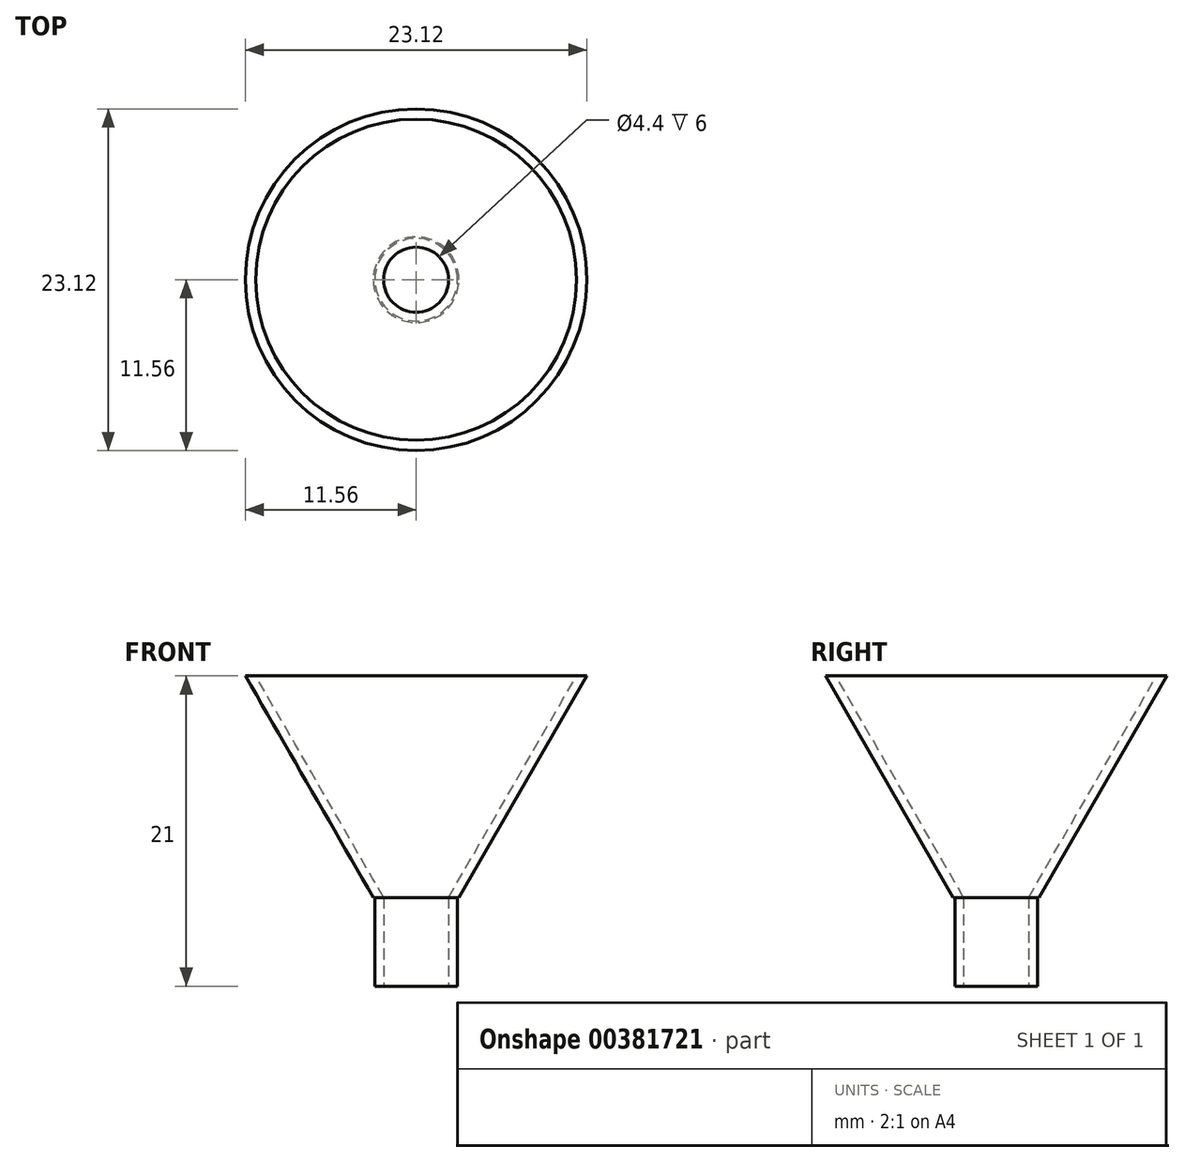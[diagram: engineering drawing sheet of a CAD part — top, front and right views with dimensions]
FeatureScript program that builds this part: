
annotation { "Feature Type Name" : "Feature", "Feature Type Description" : "" }
export const myFeature = defineFeature(function(context is Context, id is Id, definition is map)
    precondition{}
    {
        {
            var Q0;
            Q0=qCreatedBy(makeId("Top.planeOp"),FACE);
            var sketch = newSketch(context, id + "F0", { "sketchPlane" : qUnion([Q0])});
            skCircle(sketch, "E0", {"center": v(0, 0) * mm, "radius": 2.8 * mm});
            skCircle(sketch, "E1", {"center": v(0, 0) * mm, "radius": 2.2 * mm});
            skSolve(sketch);
        }
        {
            var Q0;
            Q0 = qSketchRegion(id + "F0", true);
            extrude(context, id + "F1", {"entities" : qUnion([Q0]), "depth" : 6 * mm});
        }
        {
            var Q0;
            Q0=qCreatedBy(makeId("Front.planeOp"),FACE);
            var sketch = newSketch(context, id + "F2", { "sketchPlane" : qUnion([Q0])});
            skLineSegment(sketch, "E2.0", {"start": v(-2.2, 6) * mm, "end": v(2.2, 6) * mm, "construction": true});
            skLineSegment(sketch, "E3", {"start": v(2.2, 6) * mm, "end": v(10.86, 21) * mm});
            skLineSegment(sketch, "E4", {"start": v(10.86, 21) * mm, "end": v(11.56, 21) * mm});
            skLineSegment(sketch, "E5", {"start": v(11.56, 21) * mm, "end": v(2.9, 6) * mm});
            skLineSegment(sketch, "E6", {"start": v(2.9, 6) * mm, "end": v(2.2, 6) * mm});
            skLineSegment(sketch, "E7", {"start": v(0, 6) * mm, "end": v(0, 24.89) * mm});
            skSolve(sketch);
        }
        {
            var Q0;
            Q0=makeQuery(id+"F2.imprint","IMPRINT",FACE,{"disambiguationData":[TD([[makeQuery(id+"F2.imprint","IMPRINT",EDGE,{"derivedFrom":sQuery(id+"F2.wireOp",EDGE,"E3")}),-1.0]])]});
            var Q1;
            Q1=sQuery(id+"F2.wireOp",EDGE,"E7");
            revolve(context, id + "F3", {"operationType" : NewBodyOperationType.ADD, "entities" : qUnion([Q0]), "axis" : qUnion([Q1]), "revolveType" : RevolveType.FULL});
        }
    });
